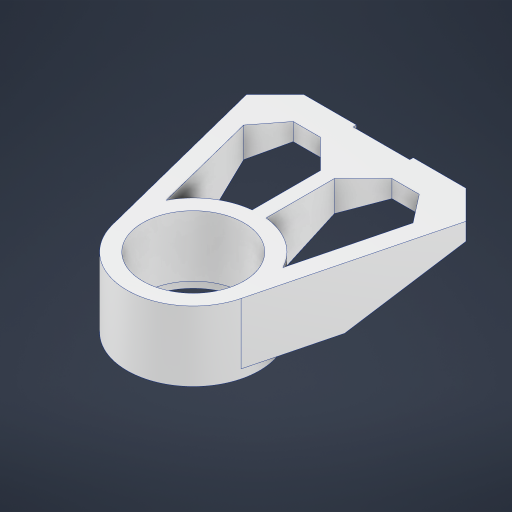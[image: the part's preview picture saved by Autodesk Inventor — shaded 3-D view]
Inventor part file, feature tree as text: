
AUTODESK INVENTOR PART (.ipt)
format: ipt  version: 2024 (Build 280153000, 153)  size: 297,472 bytes
history: native  units: mm
features: extrude x5, sketch x5, projected_geometry x5, chamfer x1
ambient origin geometry x8: Origin, YZ Plane, XZ Plane, XY Plane, X Axis, Y Axis, Z Axis, Center Point
bodies: Solid1 (feature_tree)
feature tree (16):
  extrude  "Extrusion1"  Depth=10.0mm TaperAngle=0.0deg
  extrude  "Extrusion2"  Depth=50.0mm
  extrude  "Extrusion3"  Depth=70.0mm TaperAngle=0.0deg
  extrude  "Extrusion5"  Depth=20.0mm
  chamfer  "Chamfer1"  Distance=20.0mm
  extrude  "Extrusion6"  Depth=33.0mm
  sketch  "Sketch1"  dims[d0=124.1mm d1=10.0mm d2=0.0mm]
  sketch  "Sketch2"  dims[d3=220.0mm d4=50.0mm]
  projected_geometry  "Projected Loop1"
  sketch  "Sketch3"  dims[d5=50.0mm d6=70.0mm d7=0.0mm]
  sketch  "Sketch4"  dims[d8=300.0mm d9=0.0mm d10=20.0mm]
  projected_geometry  "Projected Loop2"
  projected_geometry  "Projected Loop3"
  projected_geometry  "Projected Loop4"
  projected_geometry  "Projected Loop5"
  sketch  "Sketch7"  dims[d11=20.0mm d12=20.0mm d15=33.0mm d16=76.0mm d17=76.0mm d18=126.0mm d19=300.0mm d20=0.0mm d21=33.0mm d22=2.0mm d23=45.0deg d24=65.0mm d25=60.5mm d26=60.5mm d27=4.0mm d28=0.0mm]
